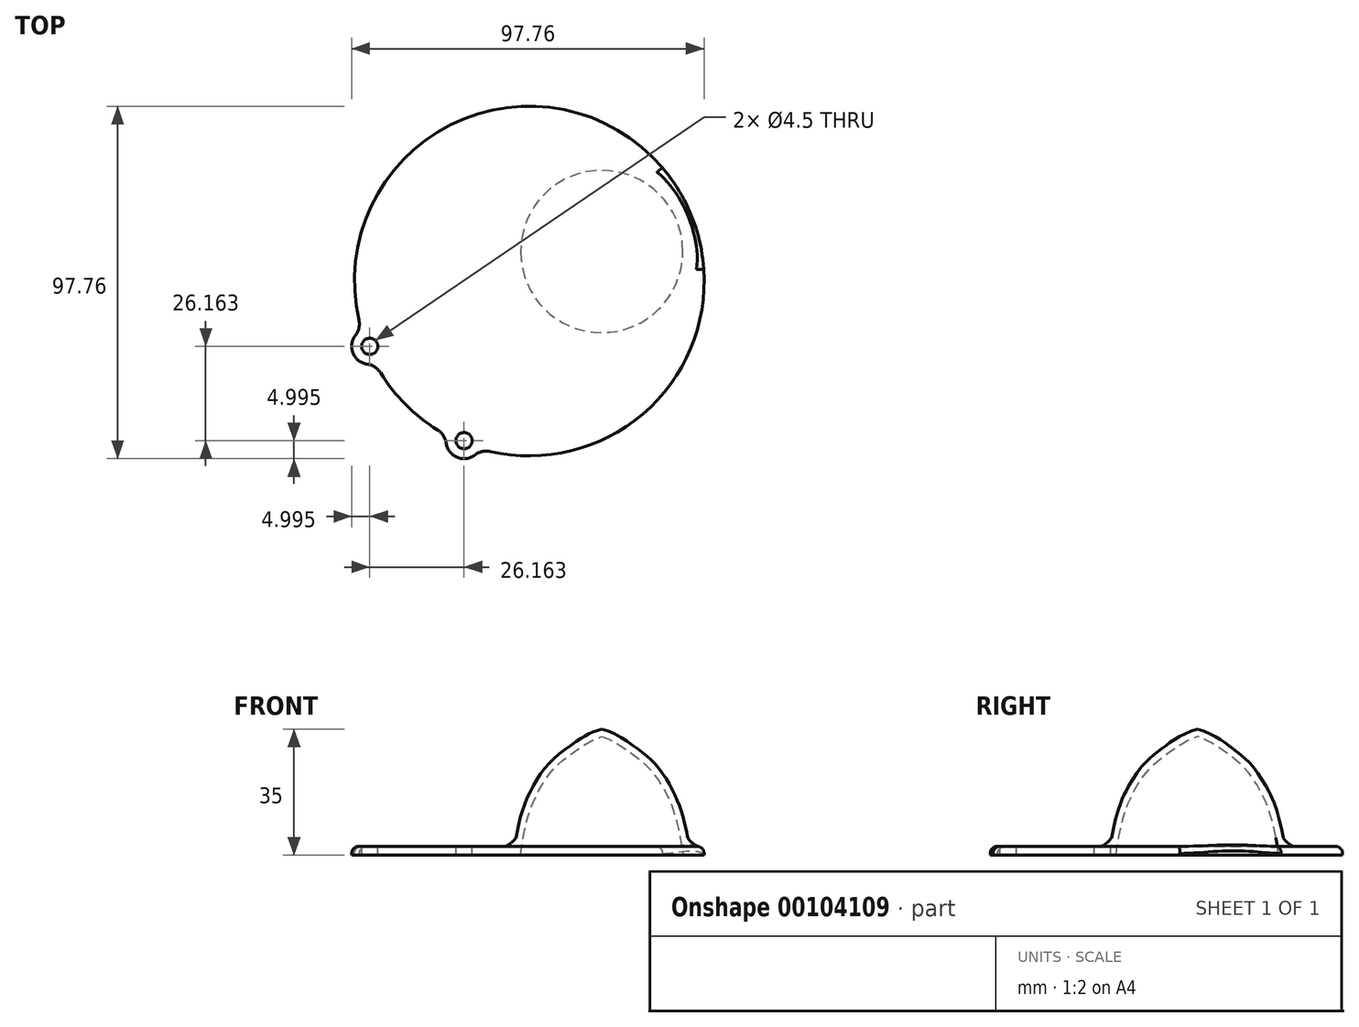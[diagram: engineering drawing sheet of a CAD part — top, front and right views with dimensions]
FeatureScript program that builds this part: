
annotation { "Feature Type Name" : "Feature", "Feature Type Description" : "" }
export const myFeature = defineFeature(function(context is Context, id is Id, definition is map)
    precondition{}
    {
        {
            var Q0;
            Q0=qCreatedBy(makeId("Top.planeOp"),FACE);
            var sketch = newSketch(context, id + "F0", { "sketchPlane" : qUnion([Q0])});
            skPoint(sketch, "E0", {"position": v(20.1, 8.2) * mm});
            skCircle(sketch, "E1", {"center": v(0, 0) * mm, "radius": 48.5 * mm});
            skSolve(sketch);
        }
        {
            var Q0;
            Q0=makeQuery(id+"F0.imprint","IMPRINT",FACE,{"disambiguationData":[TD([[makeQuery(id+"F0.imprint","IMPRINT",EDGE,{"derivedFrom":sQuery(id+"F0.wireOp",EDGE,"E1")}),1.0]])]});
            extrude(context, id + "F1", {"entities" : qUnion([Q0]), "depth" : 2.5 * mm});
        }
        {
            var Q0;
            Q0=qCreatedBy(makeId("Front.planeOp"),FACE);
            var sketch = newSketch(context, id + "F2", { "sketchPlane" : qUnion([Q0])});
            skLineSegment(sketch, "E2", {"start": v(0, 0) * mm, "end": v(24.5, 0) * mm});
            skLineSegment(sketch, "E3", {"start": v(0, 0) * mm, "end": v(0, 35) * mm});
            skFitSpline(sketch, "E4", {"points": [v(0, 35) * mm, v(9.65, 29.75) * mm, v(15.48, 24.53) * mm, v(20.26, 16.83) * mm, v(22.97, 8.92) * mm, v(24.5, 0) * mm], "startDerivative": vector(46.51, -11.17) * mm, "endDerivative": vector(0.6, -24.92) * mm});
            skSolve(sketch);
        }
        {
            var Q0;
            Q0=qCreatedBy(makeId("Top.planeOp"),FACE);
            var sketch = newSketch(context, id + "F3", { "sketchPlane" : qUnion([Q0])});
            skCircle(sketch, "E5", {"center": v(20.1, 8.2) * mm, "radius": 24 * mm});
            skSolve(sketch);
        }
        {
            var Q0;
            Q0=makeQuery(id+"F3.imprint","IMPRINT",FACE,{"disambiguationData":[TD([[makeQuery(id+"F3.imprint","IMPRINT",EDGE,{"derivedFrom":sQuery(id+"F3.wireOp",EDGE,"E5")}),1.0]])]});
            extrude(context, id + "F4", {"entities" : qUnion([Q0]), "operationType" : NewBodyOperationType.REMOVE, "depth" : 10 * mm});
        }
        {
            var Q0;
            Q0=makeQuery(id+"F2.imprint","IMPRINT",FACE,{"disambiguationData":[TD([[makeQuery(id+"F2.imprint","IMPRINT",EDGE,{"derivedFrom":sQuery(id+"F2.wireOp",EDGE,"E2")}),1.0]])]});
            var Q1;
            Q1=sQuery(id+"F2.wireOp",EDGE,"E3");
            revolve(context, id + "F5", {"entities" : qUnion([Q0]), "axis" : qUnion([Q1]), "revolveType" : RevolveType.FULL});
        }
        {
            var Q0;
            Q0=makeQuery(id+"F5.opRevolve","SWEPT_BODY",BODY,{"disambiguationData":[OSD([sQuery(id+"F2.wireOp",EDGE,"E2"),sQuery(id+"F2.wireOp",EDGE,"E3"),sQuery(id+"F2.wireOp",EDGE,"E4")])]});
            transform(context, id + "F6", {"entities" : qUnion([Q0]), "transformType" : TransformType.TRANSLATION_3D, "dx" : 20.1 * mm, "dy" : 8.2 * mm, "dz" : 0 * mm, "makeCopy" : false});
        }
        {
            var Q0;
            Q0=makeQuery(id+"F5.opRevolve","SWEPT_FACE",FACE,{"disambiguationData":[OSD([sQuery(id+"F2.wireOp",EDGE,"E2")])]});
            shell(context, id + "F7", {"entities" : qUnion([Q0]), "thickness" : 2 * mm});
        }
        {
            var Q0;
            Q0=makeQuery(id+"F1.opExtrude","SWEPT_BODY",BODY,{"disambiguationData":[OSD([sQuery(id+"F0.wireOp",EDGE,"E1")])]});
            var Q1;
            Q1=makeQuery(id+"F5.opRevolve","SWEPT_BODY",BODY,{"disambiguationData":[OSD([sQuery(id+"F2.wireOp",EDGE,"E2"),sQuery(id+"F2.wireOp",EDGE,"E3"),sQuery(id+"F2.wireOp",EDGE,"E4")])]});
            booleanBodies(context, id + "F8", {"operationType" : BooleanOperationType.UNION, "tools" : qUnion([Q0, Q1])});
        }
        {
            var Q0;
            Q0=makeQuery(id+"F8.opBoolean","INTERSECT",EDGE,{"derivedFrom":[makeQuery(id+"F1.opExtrude","CAP_FACE",FACE,{"disambiguationData":[OSD([sQuery(id+"F0.wireOp",EDGE,"E1")])],"isStart":false}),makeQuery(id+"F5.opRevolve","SWEPT_FACE",FACE,{"disambiguationData":[OSD([sQuery(id+"F2.wireOp",EDGE,"E4")])]})]});
            fillet(context, id + "F9", {"entities" : qUnion([Q0]), "radius" : 3 * mm, "tangentPropagation" : true, "rho" : .2, "crossSection" : FilletCrossSection.CONIC, "allowEdgeOverflow" : false});
        }
        {
            var Q0;
            Q0=qCreatedBy(makeId("Top.planeOp"),FACE);
            var sketch = newSketch(context, id + "F10", { "sketchPlane" : qUnion([Q0])});
            skLineSegment(sketch, "E6", {"start": v(0, 0) * mm, "end": v(-32.6, -32.6) * mm});
            skPoint(sketch, "E7", {"position": v(-32.6, -32.6) * mm});
            skSolve(sketch);
        }
        {
            var Q0;
            Q0=sQuery(id+"F10.wireOp",VERTEX,"E7");
            var Q1;
            Q1=sQuery(id+"F10.wireOp",EDGE,"E6");
            cPlane(context, id + "F11", {"entities" : qUnion([Q0, Q1]), "cplaneType" : CPlaneType.LINE_POINT, "offset" : 25 * mm, "width" : 150 * mm, "height" : 150 * mm});
        }
        {
            var Q0;
            Q0=makeQuery(id+"F1.opExtrude","CAP_FACE",FACE,{"disambiguationData":[OSD([sQuery(id+"F0.wireOp",EDGE,"E1")])],"isStart":false});
            var sketch = newSketch(context, id + "F12", { "sketchPlane" : qUnion([Q0])});
            skCircle(sketch, "E8", {"center": v(-18.1, -44.26) * mm, "radius": 2.25 * mm});
            skCircle(sketch, "E9", {"center": v(-44.26, -18.1) * mm, "radius": 2.25 * mm});
            skCircle(sketch, "E10", {"center": v(-44.26, -18.1) * mm, "radius": 5 * mm});
            skCircle(sketch, "E11", {"center": v(-18.1, -44.26) * mm, "radius": 5 * mm});
            skSolve(sketch);
        }
        {
            var Q0;
            Q0=makeQuery(id+"F12.imprint","IMPRINT",FACE,{"disambiguationData":[TD([[makeQuery(id+"F12.imprint","IMPRINT",EDGE,{"derivedFrom":sQuery(id+"F12.wireOp",EDGE,"E9")}),1.0]])]});
            var Q1;
            Q1=makeQuery(id+"F12.imprint","IMPRINT",FACE,{"disambiguationData":[TD([[makeQuery(id+"F12.imprint","IMPRINT",EDGE,{"derivedFrom":sQuery(id+"F12.wireOp",EDGE,"E8")}),1.0]])]});
            extrude(context, id + "F13", {"entities" : qUnion([Q0, Q1]), "operationType" : NewBodyOperationType.REMOVE, "oppositeDirection" : true, "depth" : 25 * mm});
        }
        {
            var Q0;
            Q0 = qSketchRegion(id + "F12", true);
            extrude(context, id + "F14", {"entities" : qUnion([Q0]), "operationType" : NewBodyOperationType.ADD, "oppositeDirection" : true, "depth" : 2.5 * mm});
        }
        {
            var Q0;
            Q0=makeQuery(id+"F14.boolean.opBoolean","INTERSECT",EDGE,{"disambiguationData":[OD(1.0)],"derivedFrom":[makeQuery(id+"F1.opExtrude","SWEPT_FACE",FACE,{"disambiguationData":[OSD([sQuery(id+"F0.wireOp",EDGE,"E1")])]}),makeQuery(id+"F14.opExtrude","SWEPT_FACE",FACE,{"disambiguationData":[OSD([sQuery(id+"F12.wireOp",EDGE,"E10")])]})]});
            var Q1;
            Q1=makeQuery(id+"F14.boolean.opBoolean","INTERSECT",EDGE,{"disambiguationData":[OD(0.0)],"derivedFrom":[makeQuery(id+"F1.opExtrude","SWEPT_FACE",FACE,{"disambiguationData":[OSD([sQuery(id+"F0.wireOp",EDGE,"E1")])]}),makeQuery(id+"F14.opExtrude","SWEPT_FACE",FACE,{"disambiguationData":[OSD([sQuery(id+"F12.wireOp",EDGE,"E10")])]})]});
            var Q2;
            Q2=makeQuery(id+"F14.boolean.opBoolean","INTERSECT",EDGE,{"disambiguationData":[OD(0.0)],"derivedFrom":[makeQuery(id+"F1.opExtrude","SWEPT_FACE",FACE,{"disambiguationData":[OSD([sQuery(id+"F0.wireOp",EDGE,"E1")])]}),makeQuery(id+"F14.opExtrude","SWEPT_FACE",FACE,{"disambiguationData":[OSD([sQuery(id+"F12.wireOp",EDGE,"E11")])]})]});
            var Q3;
            Q3=makeQuery(id+"F14.boolean.opBoolean","INTERSECT",EDGE,{"disambiguationData":[OD(1.0)],"derivedFrom":[makeQuery(id+"F1.opExtrude","SWEPT_FACE",FACE,{"disambiguationData":[OSD([sQuery(id+"F0.wireOp",EDGE,"E1")])]}),makeQuery(id+"F14.opExtrude","SWEPT_FACE",FACE,{"disambiguationData":[OSD([sQuery(id+"F12.wireOp",EDGE,"E11")])]})]});
            fillet(context, id + "F15", {"entities" : qUnion([Q0, Q1, Q2, Q3]), "radius" : 5 * mm, "tangentPropagation" : true, "allowEdgeOverflow" : false});
        }
        {
            var Q0;
            Q0=makeQuery(id+"F14.boolean.opBoolean","SPLIT",EDGE,{"disambiguationData":[OD(1.0)],"derivedFrom":makeQuery(id+"F1.opExtrude","CAP_EDGE",EDGE,{"disambiguationData":[OSD([sQuery(id+"F0.wireOp",EDGE,"E1")])],"isStart":false})});
            var Q1;
            {var subQ0=sQuery(id+"F12.wireOp",EDGE,"E10");var subQ1=sQuery(id+"F0.wireOp",EDGE,"E1");Q1=makeQuery(id+"F15.opFillet","BLEND_EDGE",EDGE,{"blendedFrom":[makeQuery(id+"F14.boolean.opBoolean","INTERSECT",EDGE,{"disambiguationData":[OD(1.0)],"derivedFrom":[makeQuery(id+"F1.opExtrude","SWEPT_FACE",FACE,{"disambiguationData":[OSD([subQ1])]}),makeQuery(id+"F14.opExtrude","SWEPT_FACE",FACE,{"disambiguationData":[OSD([subQ0])]})]}),makeQuery(id+"F14.boolean.opBoolean","MERGE",FACE,{"derivedFrom":[makeQuery(id+"F1.opExtrude","CAP_FACE",FACE,{"disambiguationData":[OSD([subQ1])],"isStart":false}),makeQuery(id+"F14.opExtrude","CAP_FACE",FACE,{"disambiguationData":[OSD([sQuery(id+"F12.wireOp",EDGE,"E8"),sQuery(id+"F12.wireOp",EDGE,"E11")])],"isStart":true}),makeQuery(id+"F14.opExtrude","CAP_FACE",FACE,{"disambiguationData":[OSD([sQuery(id+"F12.wireOp",EDGE,"E9"),subQ0])],"isStart":true})]})],"blendedInto":[makeQuery(id+"F14.boolean.opBoolean","MERGE",FACE,{"derivedFrom":[makeQuery(id+"F1.opExtrude","CAP_FACE",FACE,{"disambiguationData":[OSD([subQ1])],"isStart":false}),makeQuery(id+"F14.opExtrude","CAP_FACE",FACE,{"disambiguationData":[OSD([sQuery(id+"F12.wireOp",EDGE,"E8"),sQuery(id+"F12.wireOp",EDGE,"E11")])],"isStart":true}),makeQuery(id+"F14.opExtrude","CAP_FACE",FACE,{"disambiguationData":[OSD([sQuery(id+"F12.wireOp",EDGE,"E9"),subQ0])],"isStart":true})]})]});}
            var Q2;
            Q2=makeQuery(id+"F14.opExtrude","CAP_EDGE",EDGE,{"disambiguationData":[OSD([sQuery(id+"F12.wireOp",EDGE,"E10")])],"isStart":true});
            var Q3;
            {var subQ0=sQuery(id+"F12.wireOp",EDGE,"E10");var subQ1=sQuery(id+"F0.wireOp",EDGE,"E1");Q3=makeQuery(id+"F15.opFillet","BLEND_EDGE",EDGE,{"blendedFrom":[makeQuery(id+"F14.boolean.opBoolean","INTERSECT",EDGE,{"disambiguationData":[OD(0.0)],"derivedFrom":[makeQuery(id+"F1.opExtrude","SWEPT_FACE",FACE,{"disambiguationData":[OSD([subQ1])]}),makeQuery(id+"F14.opExtrude","SWEPT_FACE",FACE,{"disambiguationData":[OSD([subQ0])]})]}),makeQuery(id+"F14.boolean.opBoolean","MERGE",FACE,{"derivedFrom":[makeQuery(id+"F1.opExtrude","CAP_FACE",FACE,{"disambiguationData":[OSD([subQ1])],"isStart":false}),makeQuery(id+"F14.opExtrude","CAP_FACE",FACE,{"disambiguationData":[OSD([sQuery(id+"F12.wireOp",EDGE,"E8"),sQuery(id+"F12.wireOp",EDGE,"E11")])],"isStart":true}),makeQuery(id+"F14.opExtrude","CAP_FACE",FACE,{"disambiguationData":[OSD([sQuery(id+"F12.wireOp",EDGE,"E9"),subQ0])],"isStart":true})]})],"blendedInto":[makeQuery(id+"F14.boolean.opBoolean","MERGE",FACE,{"derivedFrom":[makeQuery(id+"F1.opExtrude","CAP_FACE",FACE,{"disambiguationData":[OSD([subQ1])],"isStart":false}),makeQuery(id+"F14.opExtrude","CAP_FACE",FACE,{"disambiguationData":[OSD([sQuery(id+"F12.wireOp",EDGE,"E8"),sQuery(id+"F12.wireOp",EDGE,"E11")])],"isStart":true}),makeQuery(id+"F14.opExtrude","CAP_FACE",FACE,{"disambiguationData":[OSD([sQuery(id+"F12.wireOp",EDGE,"E9"),subQ0])],"isStart":true})]})]});}
            var Q4;
            Q4=makeQuery(id+"F14.boolean.opBoolean","SPLIT",EDGE,{"disambiguationData":[OD(0.0)],"derivedFrom":makeQuery(id+"F1.opExtrude","CAP_EDGE",EDGE,{"disambiguationData":[OSD([sQuery(id+"F0.wireOp",EDGE,"E1")])],"isStart":false})});
            var Q5;
            {var subQ0=sQuery(id+"F12.wireOp",EDGE,"E11");var subQ1=sQuery(id+"F0.wireOp",EDGE,"E1");Q5=makeQuery(id+"F15.opFillet","BLEND_EDGE",EDGE,{"blendedFrom":[makeQuery(id+"F14.boolean.opBoolean","INTERSECT",EDGE,{"disambiguationData":[OD(0.0)],"derivedFrom":[makeQuery(id+"F1.opExtrude","SWEPT_FACE",FACE,{"disambiguationData":[OSD([subQ1])]}),makeQuery(id+"F14.opExtrude","SWEPT_FACE",FACE,{"disambiguationData":[OSD([subQ0])]})]}),makeQuery(id+"F14.boolean.opBoolean","MERGE",FACE,{"derivedFrom":[makeQuery(id+"F1.opExtrude","CAP_FACE",FACE,{"disambiguationData":[OSD([subQ1])],"isStart":false}),makeQuery(id+"F14.opExtrude","CAP_FACE",FACE,{"disambiguationData":[OSD([sQuery(id+"F12.wireOp",EDGE,"E8"),subQ0])],"isStart":true}),makeQuery(id+"F14.opExtrude","CAP_FACE",FACE,{"disambiguationData":[OSD([sQuery(id+"F12.wireOp",EDGE,"E9"),sQuery(id+"F12.wireOp",EDGE,"E10")])],"isStart":true})]})],"blendedInto":[makeQuery(id+"F14.boolean.opBoolean","MERGE",FACE,{"derivedFrom":[makeQuery(id+"F1.opExtrude","CAP_FACE",FACE,{"disambiguationData":[OSD([subQ1])],"isStart":false}),makeQuery(id+"F14.opExtrude","CAP_FACE",FACE,{"disambiguationData":[OSD([sQuery(id+"F12.wireOp",EDGE,"E8"),subQ0])],"isStart":true}),makeQuery(id+"F14.opExtrude","CAP_FACE",FACE,{"disambiguationData":[OSD([sQuery(id+"F12.wireOp",EDGE,"E9"),sQuery(id+"F12.wireOp",EDGE,"E10")])],"isStart":true})]})]});}
            var Q6;
            Q6=makeQuery(id+"F14.opExtrude","CAP_EDGE",EDGE,{"disambiguationData":[OSD([sQuery(id+"F12.wireOp",EDGE,"E11")])],"isStart":true});
            var Q7;
            {var subQ0=sQuery(id+"F12.wireOp",EDGE,"E11");var subQ1=sQuery(id+"F0.wireOp",EDGE,"E1");Q7=makeQuery(id+"F15.opFillet","BLEND_EDGE",EDGE,{"blendedFrom":[makeQuery(id+"F14.boolean.opBoolean","INTERSECT",EDGE,{"disambiguationData":[OD(1.0)],"derivedFrom":[makeQuery(id+"F1.opExtrude","SWEPT_FACE",FACE,{"disambiguationData":[OSD([subQ1])]}),makeQuery(id+"F14.opExtrude","SWEPT_FACE",FACE,{"disambiguationData":[OSD([subQ0])]})]}),makeQuery(id+"F14.boolean.opBoolean","MERGE",FACE,{"derivedFrom":[makeQuery(id+"F1.opExtrude","CAP_FACE",FACE,{"disambiguationData":[OSD([subQ1])],"isStart":false}),makeQuery(id+"F14.opExtrude","CAP_FACE",FACE,{"disambiguationData":[OSD([sQuery(id+"F12.wireOp",EDGE,"E8"),subQ0])],"isStart":true}),makeQuery(id+"F14.opExtrude","CAP_FACE",FACE,{"disambiguationData":[OSD([sQuery(id+"F12.wireOp",EDGE,"E9"),sQuery(id+"F12.wireOp",EDGE,"E10")])],"isStart":true})]})],"blendedInto":[makeQuery(id+"F14.boolean.opBoolean","MERGE",FACE,{"derivedFrom":[makeQuery(id+"F1.opExtrude","CAP_FACE",FACE,{"disambiguationData":[OSD([subQ1])],"isStart":false}),makeQuery(id+"F14.opExtrude","CAP_FACE",FACE,{"disambiguationData":[OSD([sQuery(id+"F12.wireOp",EDGE,"E8"),subQ0])],"isStart":true}),makeQuery(id+"F14.opExtrude","CAP_FACE",FACE,{"disambiguationData":[OSD([sQuery(id+"F12.wireOp",EDGE,"E9"),sQuery(id+"F12.wireOp",EDGE,"E10")])],"isStart":true})]})]});}
            var Q8;
            Q8=makeQuery(id+"F13.boolean.opBoolean","COPY",EDGE,{"derivedFrom":makeQuery(id+"F13.opExtrude","CAP_EDGE",EDGE,{"disambiguationData":[OSD([sQuery(id+"F12.wireOp",EDGE,"E9")])],"isStart":true})});
            var Q9;
            Q9=makeQuery(id+"F13.boolean.opBoolean","COPY",EDGE,{"derivedFrom":makeQuery(id+"F13.opExtrude","CAP_EDGE",EDGE,{"disambiguationData":[OSD([sQuery(id+"F12.wireOp",EDGE,"E8")])],"isStart":true})});
            fillet(context, id + "F16", {"entities" : qUnion([Q0, Q1, Q2, Q3, Q4, Q5, Q6, Q7, Q8, Q9]), "radius" : 2 * mm, "tangentPropagation" : true, "allowEdgeOverflow" : false});
        }
    });
